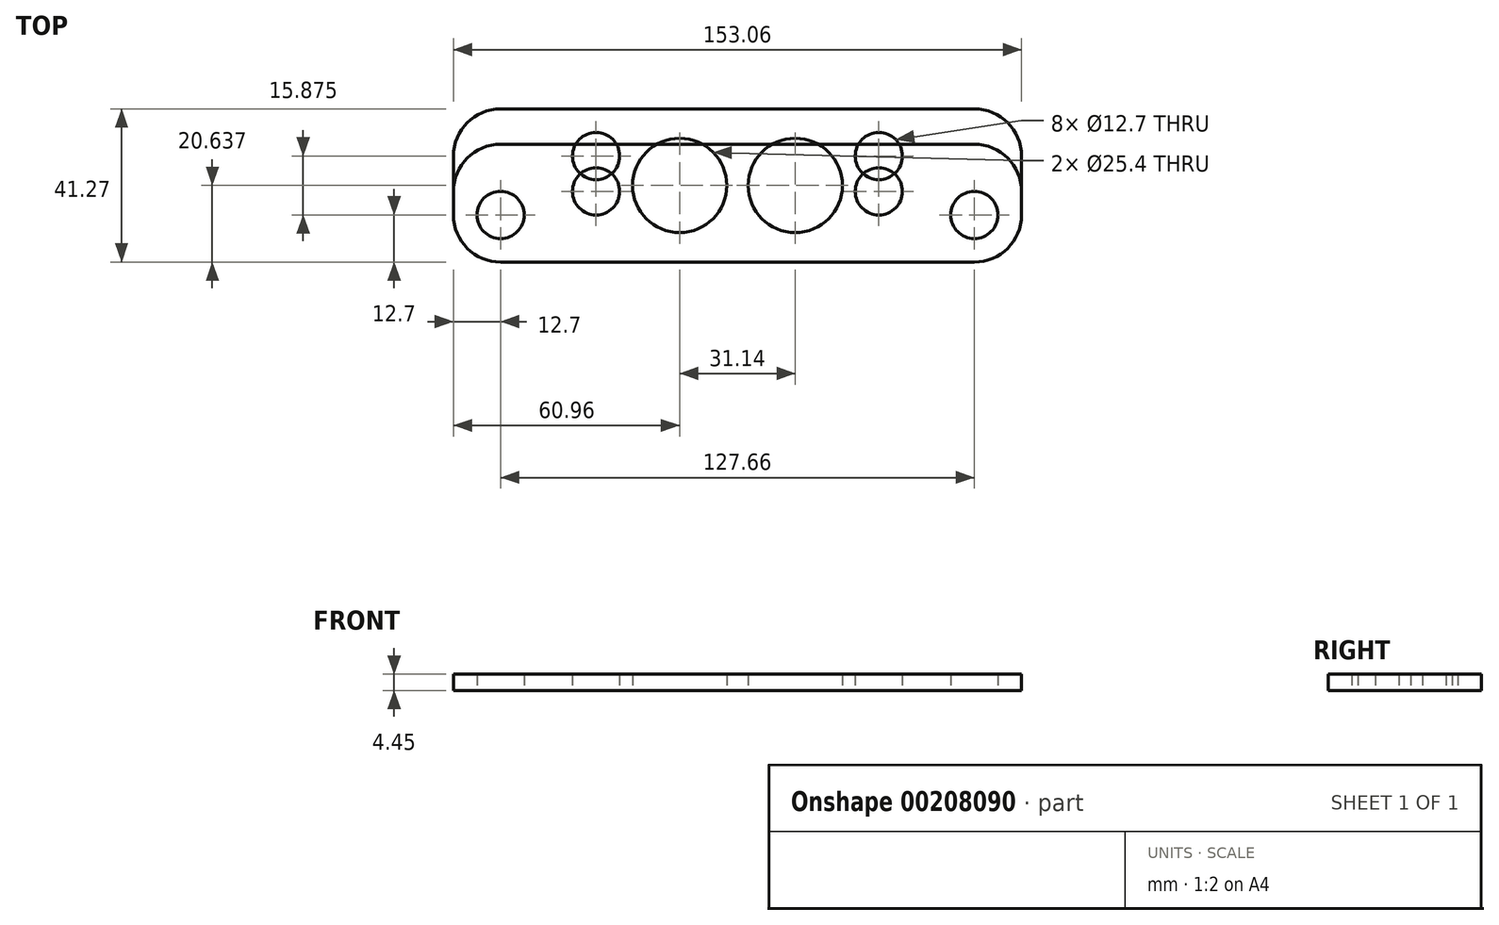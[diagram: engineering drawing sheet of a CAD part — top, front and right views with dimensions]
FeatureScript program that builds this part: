
annotation { "Feature Type Name" : "Feature", "Feature Type Description" : "" }
export const myFeature = defineFeature(function(context is Context, id is Id, definition is map)
    precondition{}
    {
        {
            var Q0;
            Q0=qCreatedBy(makeId("Top.planeOp"),FACE);
            var sketch = newSketch(context, id + "F0", { "sketchPlane" : qUnion([Q0])});
            skCircle(sketch, "E0", {"center": v(0, 0) * mm, "radius": 6.35 * mm});
            skCircle(sketch, "E1", {"center": v(127.66, 0) * mm, "radius": 6.35 * mm});
            skCircle(sketch, "E2", {"center": v(25.73, 6.35) * mm, "radius": 6.35 * mm});
            skCircle(sketch, "E3", {"center": v(101.93, 6.35) * mm, "radius": 6.35 * mm});
            skLineSegment(sketch, "E4", {"start": v(25.73, 6.35) * mm, "end": v(101.93, 6.35) * mm, "construction": true});
            skLineSegment(sketch, "E5", {"start": v(0, 0) * mm, "end": v(127.66, 0) * mm, "construction": true});
            skPoint(sketch, "E6", {"position": v(63.83, 6.35) * mm});
            skPoint(sketch, "E7", {"position": v(63.83, 0) * mm});
            skLineSegment(sketch, "E8.bottom", {"start": v(0, 19.05) * mm, "end": v(127.66, 19.05) * mm});
            skLineSegment(sketch, "E8.top", {"start": v(0, -12.7) * mm, "end": v(127.66, -12.7) * mm});
            skLineSegment(sketch, "E8.left", {"start": v(-12.7, 6.35) * mm, "end": v(-12.7, 0) * mm});
            skLineSegment(sketch, "E8.right", {"start": v(140.36, 6.35) * mm, "end": v(140.36, 0) * mm});
            skPoint(sketch, "E9.visualSharp", {"position": v(-12.7, 19.05) * mm});
            skArc(sketch, "E9.filletArc", {"start": v(0, 19.05) * mm, "mid": v(-8.98, 15.33) * mm, "end": v(-12.7, 6.35) * mm});
            skPoint(sketch, "E10.visualSharp", {"position": v(-12.7, -12.7) * mm});
            skArc(sketch, "E10.filletArc", {"start": v(-12.7, 0) * mm, "mid": v(-8.98, -8.98) * mm, "end": v(0, -12.7) * mm});
            skPoint(sketch, "E11.visualSharp", {"position": v(140.36, 19.05) * mm});
            skArc(sketch, "E11.filletArc", {"start": v(140.36, 6.35) * mm, "mid": v(136.64, 15.33) * mm, "end": v(127.66, 19.05) * mm});
            skPoint(sketch, "E12.visualSharp", {"position": v(140.36, -12.7) * mm});
            skArc(sketch, "E12.filletArc", {"start": v(127.66, -12.7) * mm, "mid": v(136.64, -8.98) * mm, "end": v(140.36, 0) * mm});
            skSolve(sketch);
        }
        {
            var Q0;
            Q0=makeQuery(id+"F0.imprint","IMPRINT",FACE,{"disambiguationData":[TD([[makeQuery(id+"F0.imprint","IMPRINT",EDGE,{"derivedFrom":sQuery(id+"F0.wireOp",EDGE,"E0")}),-1.0]])]});
            extrude(context, id + "F1", {"entities" : qUnion([Q0]), "depth" : 4.44 * mm});
        }
        {
            var Q0;
            Q0=qCreatedBy(makeId("Top.planeOp"),FACE);
            var sketch = newSketch(context, id + "F2", { "sketchPlane" : qUnion([Q0])});
            skCircle(sketch, "E13", {"center": v(0, 0) * mm, "radius": 6.35 * mm});
            skCircle(sketch, "E14", {"center": v(127.66, 0) * mm, "radius": 6.35 * mm});
            skCircle(sketch, "E15", {"center": v(25.73, 15.88) * mm, "radius": 6.35 * mm});
            skCircle(sketch, "E16", {"center": v(101.93, 15.88) * mm, "radius": 6.35 * mm});
            skLineSegment(sketch, "E17", {"start": v(25.73, 15.88) * mm, "end": v(101.93, 15.88) * mm, "construction": true});
            skLineSegment(sketch, "E18", {"start": v(0, 0) * mm, "end": v(127.66, 0) * mm, "construction": true});
            skPoint(sketch, "E19", {"position": v(63.83, 15.88) * mm});
            skPoint(sketch, "E20", {"position": v(63.83, 0) * mm});
            skLineSegment(sketch, "E21.bottom", {"start": v(0, 28.58) * mm, "end": v(127.66, 28.58) * mm});
            skLineSegment(sketch, "E21.top", {"start": v(0, -12.7) * mm, "end": v(127.66, -12.7) * mm});
            skLineSegment(sketch, "E21.left", {"start": v(-12.7, 15.88) * mm, "end": v(-12.7, 0) * mm});
            skLineSegment(sketch, "E21.right", {"start": v(140.36, 15.88) * mm, "end": v(140.36, 0) * mm});
            skPoint(sketch, "E22.visualSharp", {"position": v(-12.7, 28.58) * mm});
            skArc(sketch, "E22.filletArc", {"start": v(0, 28.58) * mm, "mid": v(-8.98, 24.86) * mm, "end": v(-12.7, 15.88) * mm});
            skPoint(sketch, "E23.visualSharp", {"position": v(-12.7, -12.7) * mm});
            skArc(sketch, "E23.filletArc", {"start": v(-12.7, 0) * mm, "mid": v(-8.98, -8.98) * mm, "end": v(0, -12.7) * mm});
            skPoint(sketch, "E24.visualSharp", {"position": v(140.36, 28.58) * mm});
            skArc(sketch, "E24.filletArc", {"start": v(140.36, 15.88) * mm, "mid": v(136.64, 24.86) * mm, "end": v(127.66, 28.58) * mm});
            skPoint(sketch, "E25.visualSharp", {"position": v(140.36, -12.7) * mm});
            skArc(sketch, "E25.filletArc", {"start": v(127.66, -12.7) * mm, "mid": v(136.64, -8.98) * mm, "end": v(140.36, 0) * mm});
            skCircle(sketch, "E26", {"center": v(48.26, 7.94) * mm, "radius": 12.7 * mm});
            skCircle(sketch, "E27", {"center": v(79.4, 7.94) * mm, "radius": 12.7 * mm});
            skSolve(sketch);
        }
        {
            var Q0;
            Q0=makeQuery(id+"F2.imprint","IMPRINT",FACE,{"disambiguationData":[TD([[makeQuery(id+"F2.imprint","IMPRINT",EDGE,{"derivedFrom":sQuery(id+"F2.wireOp",EDGE,"E13")}),-1.0]])]});
            extrude(context, id + "F3", {"entities" : qUnion([Q0]), "depth" : 4.44 * mm});
        }
    });
